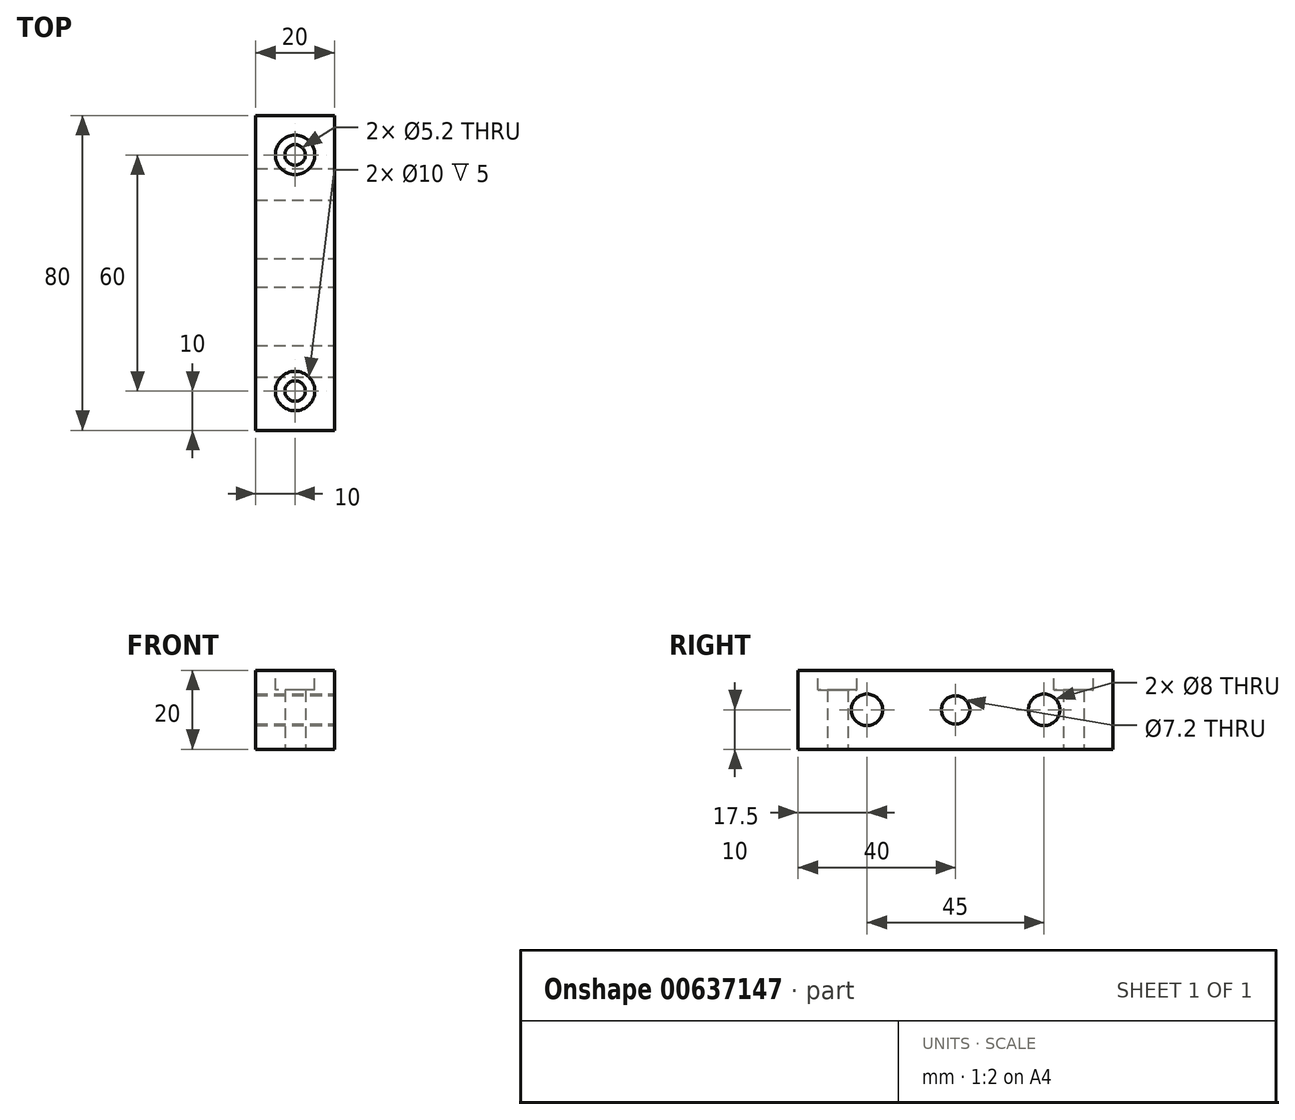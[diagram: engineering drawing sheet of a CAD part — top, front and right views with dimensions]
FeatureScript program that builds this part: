
annotation { "Feature Type Name" : "Feature", "Feature Type Description" : "" }
export const myFeature = defineFeature(function(context is Context, id is Id, definition is map)
    precondition{}
    {
        {
            var Q0;
            Q0=qCreatedBy(makeId("Top.planeOp"),FACE);
            var sketch = newSketch(context, id + "F0", { "sketchPlane" : qUnion([Q0])});
            skLineSegment(sketch, "E0.bottom", {"start": v(10, -40) * mm, "end": v(-10, -40) * mm});
            skLineSegment(sketch, "E0.top", {"start": v(10, 40) * mm, "end": v(-10, 40) * mm});
            skLineSegment(sketch, "E0.left", {"start": v(10, -40) * mm, "end": v(10, 40) * mm});
            skLineSegment(sketch, "E0.right", {"start": v(-10, -40) * mm, "end": v(-10, 40) * mm});
            skPoint(sketch, "E0.middle", {"position": v(0, 0) * mm});
            skLineSegment(sketch, "E1", {"start": v(0, 40) * mm, "end": v(0, -40) * mm, "construction": true});
            skCircle(sketch, "E2", {"center": v(0, 30) * mm, "radius": 2.6 * mm});
            skCircle(sketch, "E3", {"center": v(0, -30) * mm, "radius": 2.6 * mm});
            skSolve(sketch);
        }
        {
            var Q0;
            Q0=makeQuery(id+"F0.imprint","IMPRINT",FACE,{"disambiguationData":[TD([[makeQuery(id+"F0.imprint","IMPRINT",EDGE,{"derivedFrom":sQuery(id+"F0.wireOp",EDGE,"E0.bottom")}),-1.0]])]});
            extrude(context, id + "F1", {"entities" : qUnion([Q0]), "depth" : 20 * mm, "offsetDistance" : 25 * mm});
        }
        {
            var Q0;
            Q0=makeQuery(id+"F1.opExtrude","CAP_FACE",FACE,{"disambiguationData":[OSD([sQuery(id+"F0.wireOp",EDGE,"E0.bottom"),sQuery(id+"F0.wireOp",EDGE,"E0.top"),sQuery(id+"F0.wireOp",EDGE,"E0.left"),sQuery(id+"F0.wireOp",EDGE,"E0.right"),sQuery(id+"F0.wireOp",EDGE,"E2"),sQuery(id+"F0.wireOp",EDGE,"E3")])],"isStart":false});
            var sketch = newSketch(context, id + "F2", { "sketchPlane" : qUnion([Q0])});
            skCircle(sketch, "E4", {"center": v(0, 30) * mm, "radius": 5 * mm});
            skCircle(sketch, "E5", {"center": v(0, -30) * mm, "radius": 5 * mm});
            skSolve(sketch);
        }
        {
            var Q0;
            Q0 = qSketchRegion(id + "F2", true);
            extrude(context, id + "F3", {"entities" : qUnion([Q0]), "operationType" : NewBodyOperationType.REMOVE, "oppositeDirection" : true, "depth" : 5 * mm, "offsetDistance" : 25 * mm});
        }
        {
            var Q0;
            Q0=makeQuery(id+"F1.opExtrude","SWEPT_FACE",FACE,{"disambiguationData":[OSD([sQuery(id+"F0.wireOp",EDGE,"E0.left")])]});
            var sketch = newSketch(context, id + "F4", { "sketchPlane" : qUnion([Q0])});
            skLineSegment(sketch, "E6", {"start": v(-40, 10) * mm, "end": v(40, 10) * mm, "construction": true});
            skCircle(sketch, "E7", {"center": v(-22.5, 10) * mm, "radius": 4 * mm});
            skCircle(sketch, "E8", {"center": v(22.5, 10) * mm, "radius": 4 * mm});
            skCircle(sketch, "E9", {"center": v(0, 10) * mm, "radius": 3.6 * mm});
            skSolve(sketch);
        }
        {
            var Q0;
            Q0=makeQuery(id+"F4.imprint","IMPRINT",FACE,{"disambiguationData":[TD([[makeQuery(id+"F4.imprint","IMPRINT",EDGE,{"derivedFrom":sQuery(id+"F4.wireOp",EDGE,"E7")}),1.0]])]});
            var Q1;
            Q1=makeQuery(id+"F4.imprint","IMPRINT",FACE,{"disambiguationData":[TD([[makeQuery(id+"F4.imprint","IMPRINT",EDGE,{"derivedFrom":sQuery(id+"F4.wireOp",EDGE,"E8")}),1.0]])]});
            var Q2;
            Q2=makeQuery(id+"F4.imprint","IMPRINT",FACE,{"disambiguationData":[TD([[makeQuery(id+"F4.imprint","IMPRINT",EDGE,{"derivedFrom":sQuery(id+"F4.wireOp",EDGE,"E9")}),1.0]])]});
            extrude(context, id + "F5", {"entities" : qUnion([Q0, Q1, Q2]), "operationType" : NewBodyOperationType.REMOVE, "oppositeDirection" : true, "depth" : 25 * mm, "offsetDistance" : 25 * mm});
        }
    });
